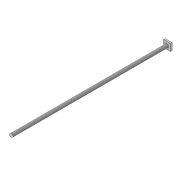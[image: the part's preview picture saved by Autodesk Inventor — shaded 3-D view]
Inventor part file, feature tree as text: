
AUTODESK INVENTOR PART (.ipt)
format: ipt  version: 2019 (Build 230136000, 136)  size: 90,624 bytes
history: native  units: mm
features: sketch x3, extrude x2, thread x1
ambient origin geometry x8: Origin, YZ Plane, XZ Plane, XY Plane, X Axis, Y Axis, Z Axis, Center Point
bodies: Solid1 (feature_tree)
feature tree (6):
  extrude  "Extrusion1"  Depth=20.0mm
  sketch  "Sketch2"  dims[d4=5.0mm d5=0.0mm d6=10.0mm d7=10.0mm]
  extrude  "Extrusion2"  Depth=10.0mm
  thread  "Thread1"  [1 undecoded]
  sketch  "Sketch1"  dims[d2=20.0mm d3=20.0mm]
  sketch  "Sketch3"  dims[d8=10.0mm d9=450.0mm d10=0.0mm d11=10.0mm d12=0.0mm]
note: 1 required parameter value undecoded (feature->parameter linkage not recoverable at this tier; creation-order binding heuristic only, values carry confidence <= 0.55)
